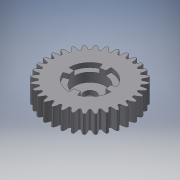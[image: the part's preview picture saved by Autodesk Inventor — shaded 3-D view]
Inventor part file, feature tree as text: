
AUTODESK INVENTOR PART (.ipt)
format: ipt  version: 2017 (Build 210142000, 142)  size: 291,840 bytes
history: native  units: mm
features: extrude x5, sketch x4, pattern_circular x2
ambient origin geometry x8: Origin, YZ Plane, XZ Plane, XY Plane, X Axis, Y Axis, Z Axis, Center Point
bodies: Solid1 (feature_tree)
feature tree (11):
  sketch  "Sketch1"  dims[d0=20.0mm d1=0.0mm]
  extrude  "Extrusion1"  TaperAngle=0.0deg  [1 undecoded]
  extrude  "Extrusion2"  Depth=10.0mm TaperAngle=360.0deg
  pattern_circular  "Circular Pattern1"  [2 undecoded]
  extrude  "Extrusion3"  Depth=15.0mm TaperAngle=0.0deg
  extrude  "Extrusion4"  Depth=5.0mm
  extrude  "Extrusion5"  Depth=5.0mm
  pattern_circular  "Circular Pattern2"  [2 undecoded]
  sketch  "Sketch2"  dims[d2=10.0mm d3=0.0mm d4=320.0mm d5=360.0deg]
  sketch  "Sketch3"  dims[d7=13.5mm]
  sketch  "Sketch4"  dims[d8=10.0mm d9=0.0mm d10=35.0mm d11=15.0mm d12=0.0mm d13=6.0mm d14=12.217305mm d15=5.0mm d16=0.0mm d17=40.0mm d18=360.0deg]
note: 5 required parameter values undecoded (feature->parameter linkage not recoverable at this tier; creation-order binding heuristic only, values carry confidence <= 0.55)
